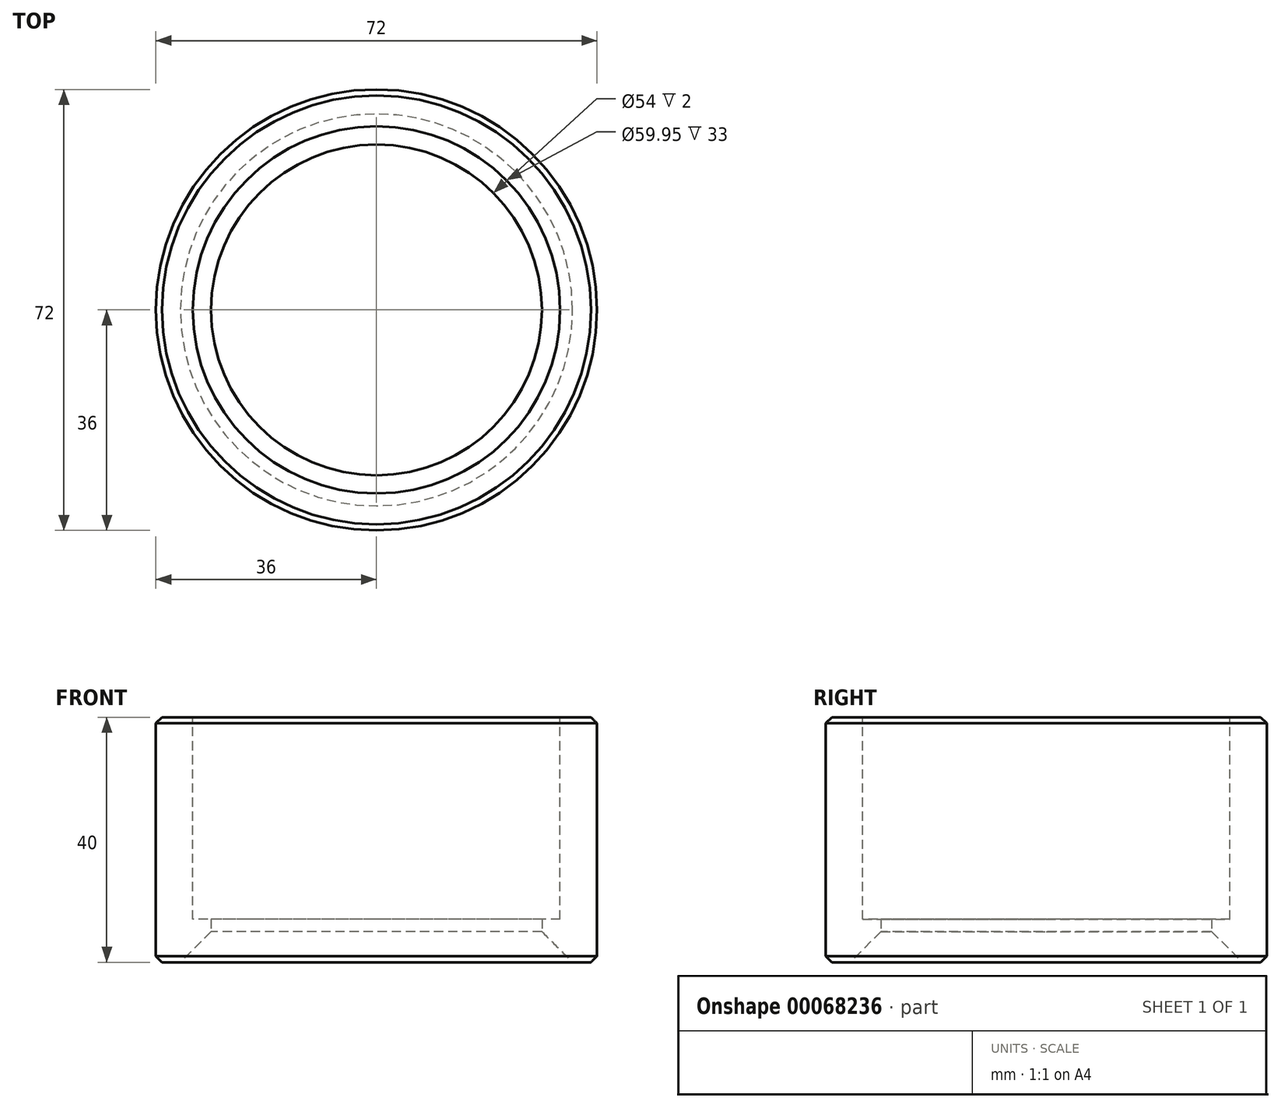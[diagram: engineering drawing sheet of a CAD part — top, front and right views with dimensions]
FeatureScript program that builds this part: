
annotation { "Feature Type Name" : "Feature", "Feature Type Description" : "" }
export const myFeature = defineFeature(function(context is Context, id is Id, definition is map)
    precondition{}
    {
        {
            var Q0;
            Q0=qCreatedBy(makeId("Top.planeOp"),FACE);
            var sketch = newSketch(context, id + "F0", { "sketchPlane" : qUnion([Q0])});
            skCircle(sketch, "E0", {"center": v(0, 0) * mm, "radius": 36 * mm});
            skCircle(sketch, "E1", {"center": v(0, 0) * mm, "radius": 27 * mm});
            skSolve(sketch);
        }
        {
            var Q0;
            Q0 = qSketchRegion(id + "F0", true);
            extrude(context, id + "F1", {"entities" : qUnion([Q0]), "depth" : 40 * mm});
        }
        {
            var Q0;
            Q0=makeQuery(id+"F1.opExtrude","CAP_FACE",FACE,{"disambiguationData":[OSD([sQuery(id+"F0.wireOp",EDGE,"E0"),sQuery(id+"F0.wireOp",EDGE,"E1")])],"isStart":false});
            var sketch = newSketch(context, id + "F2", { "sketchPlane" : qUnion([Q0])});
            skCircle(sketch, "E2", {"center": v(0, 0) * mm, "radius": 29.98 * mm});
            skSolve(sketch);
        }
        {
            var Q0;
            Q0 = qSketchRegion(id + "F2", true);
            extrude(context, id + "F3", {"entities" : qUnion([Q0]), "operationType" : NewBodyOperationType.REMOVE, "oppositeDirection" : true, "depth" : 33 * mm});
        }
        {
            var Q0;
            Q0=makeQuery(id+"F1.opExtrude","CAP_EDGE",EDGE,{"disambiguationData":[OSD([sQuery(id+"F0.wireOp",EDGE,"E1")])],"isStart":true});
            chamfer(context, id + "F4", {"entities" : qUnion([Q0]), "width" : 5 * mm, "tangentPropagation" : true});
        }
        {
            var Q0;
            Q0=makeQuery(id+"F1.opExtrude","CAP_EDGE",EDGE,{"disambiguationData":[OSD([sQuery(id+"F0.wireOp",EDGE,"E0")])],"isStart":true});
            var Q1;
            Q1=makeQuery(id+"F1.opExtrude","CAP_EDGE",EDGE,{"disambiguationData":[OSD([sQuery(id+"F0.wireOp",EDGE,"E0")])],"isStart":false});
            var Q2;
            Q2=makeQuery(id+"F3.boolean.opBoolean","COPY",EDGE,{"derivedFrom":makeQuery(id+"F3.opExtrude","CAP_EDGE",EDGE,{"disambiguationData":[OSD([sQuery(id+"F2.wireOp",EDGE,"E2")])],"isStart":true})});
            chamfer(context, id + "F5", {"entities" : qUnion([Q0, Q1, Q2]), "width" : 1 * mm, "tangentPropagation" : true});
        }
    });
